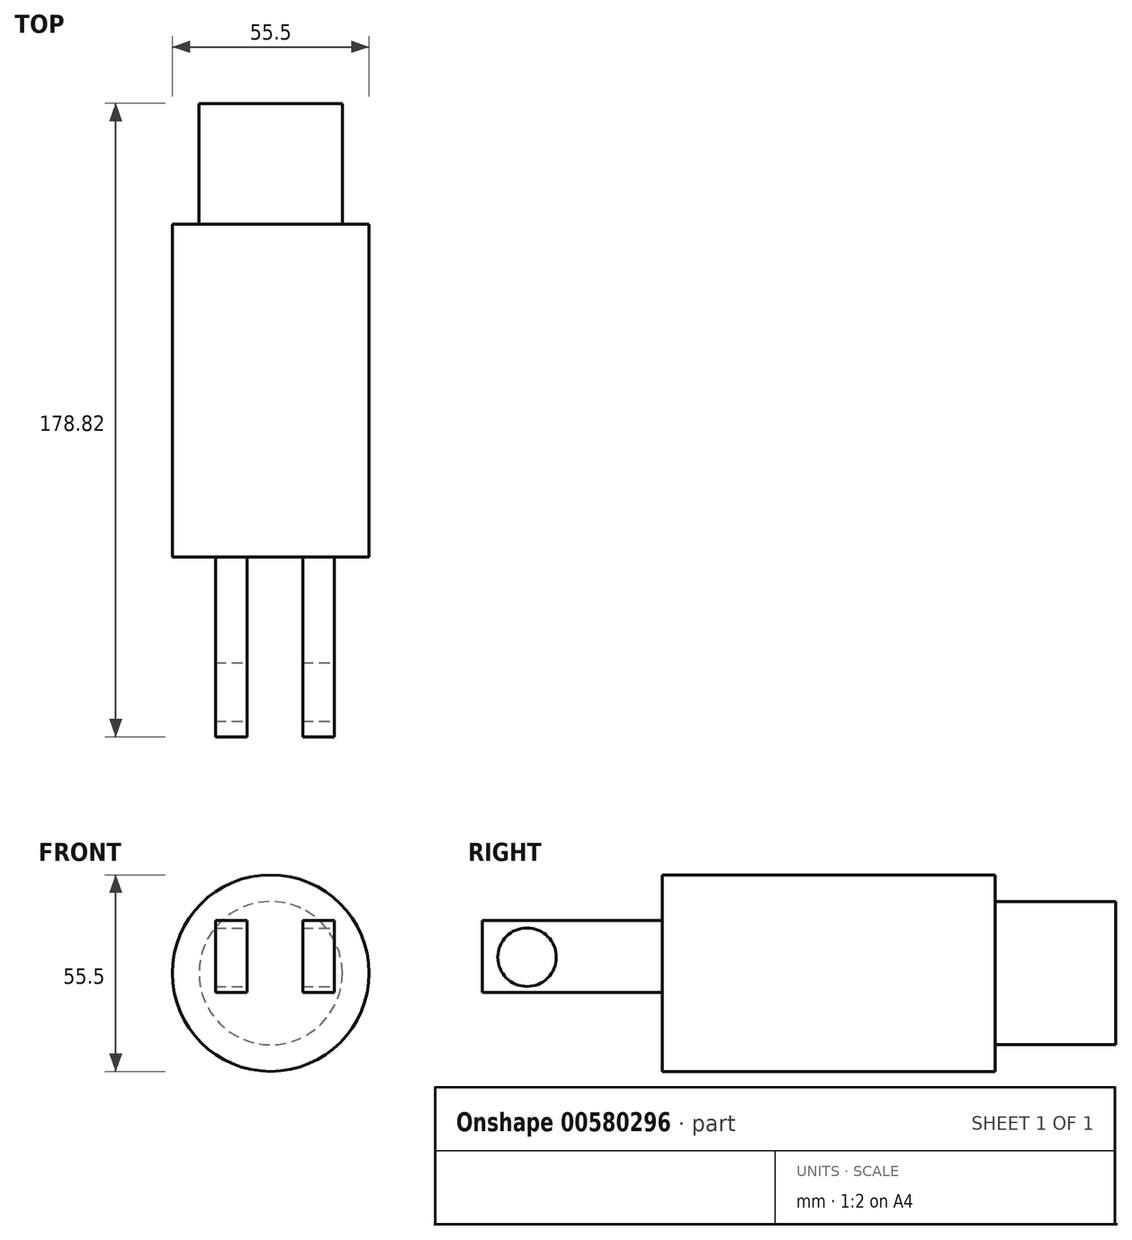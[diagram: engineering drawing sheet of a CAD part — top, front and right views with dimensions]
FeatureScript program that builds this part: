
annotation { "Feature Type Name" : "Feature", "Feature Type Description" : "" }
export const myFeature = defineFeature(function(context is Context, id is Id, definition is map)
    precondition{}
    {
        {
            var Q0;
            Q0=qCreatedBy(makeId("Front.planeOp"),FACE);
            var sketch = newSketch(context, id + "F0", { "sketchPlane" : qUnion([Q0])});
            skCircle(sketch, "E0", {"center": v(0, 0) * mm, "radius": 27.75 * mm});
            skSolve(sketch);
        }
        {
            var Q0;
            Q0 = qSketchRegion(id + "F0", true);
            extrude(context, id + "F1", {"entities" : qUnion([Q0]), "oppositeDirection" : true, "depth" : 93.98 * mm, "offsetDistance" : 25.4 * mm});
        }
        {
            var Q0;
            Q0=makeQuery(id+"F1.opExtrude","CAP_FACE",FACE,{"disambiguationData":[OSD([sQuery(id+"F0.wireOp",EDGE,"E0")])],"isStart":false});
            var sketch = newSketch(context, id + "F2", { "sketchPlane" : qUnion([Q0])});
            skCircle(sketch, "E1", {"center": v(0, 0) * mm, "radius": 20.22 * mm});
            skSolve(sketch);
        }
        {
            var Q0;
            Q0 = qSketchRegion(id + "F2", true);
            extrude(context, id + "F3", {"entities" : qUnion([Q0]), "operationType" : NewBodyOperationType.ADD, "depth" : 34.04 * mm, "offsetDistance" : 25.4 * mm});
        }
        {
            var Q0;
            Q0=qCreatedBy(makeId("Front.planeOp"),FACE);
            var sketch = newSketch(context, id + "F4", { "sketchPlane" : qUnion([Q0])});
            skLineSegment(sketch, "E2", {"start": v(0, 0) * mm, "end": v(-9.1, 0) * mm});
            skLineSegment(sketch, "E3", {"start": v(-9.1, 0) * mm, "end": v(0, 0) * mm});
            skLineSegment(sketch, "E4", {"start": v(0, 0) * mm, "end": v(9.05, 0) * mm});
            skLineSegment(sketch, "E5.bottom", {"start": v(-6.69, -5.45) * mm, "end": v(-15.58, -5.45) * mm});
            skLineSegment(sketch, "E5.top", {"start": v(-6.69, 14.87) * mm, "end": v(-15.58, 14.87) * mm});
            skLineSegment(sketch, "E5.left", {"start": v(-6.69, -5.45) * mm, "end": v(-6.69, 14.87) * mm});
            skLineSegment(sketch, "E5.right", {"start": v(-15.58, -5.45) * mm, "end": v(-15.58, 14.87) * mm});
            skLineSegment(sketch, "E6.bottom", {"start": v(9.05, -5.45) * mm, "end": v(17.94, -5.45) * mm});
            skLineSegment(sketch, "E6.top", {"start": v(9.05, 14.87) * mm, "end": v(17.94, 14.87) * mm});
            skLineSegment(sketch, "E6.left", {"start": v(9.05, -5.45) * mm, "end": v(9.05, 14.87) * mm});
            skLineSegment(sketch, "E6.right", {"start": v(17.94, -5.45) * mm, "end": v(17.94, 14.87) * mm});
            skSolve(sketch);
        }
        {
            var Q0;
            Q0 = qSketchRegion(id + "F4", true);
            extrude(context, id + "F5", {"entities" : qUnion([Q0]), "operationType" : NewBodyOperationType.ADD, "depth" : 50.8 * mm, "offsetDistance" : 25.4 * mm});
        }
        {
            var Q0;
            Q0=qCreatedBy(makeId("Right.planeOp"),FACE);
            var sketch = newSketch(context, id + "F6", { "sketchPlane" : qUnion([Q0])});
            skCircle(sketch, "E7", {"center": v(-38.16, 4.5) * mm, "radius": 8.26 * mm});
            skSolve(sketch);
        }
        {
            var Q0;
            Q0=sQuery(id+"F6.wireOp",EDGE,"E7");
            extrude(context, id + "F7", {"bodyType" : ToolBodyType.SURFACE, "surfaceEntities" : qUnion([Q0]), "depth" : 25.4 * mm, "offsetDistance" : 25.4 * mm, "hasSecondDirection" : true, "secondDirectionOppositeDirection" : true, "secondDirectionDepth" : 25.4 * mm});
        }
        {
            var Q0;
            Q0 = qSketchRegion(id + "F6", true);
            extrude(context, id + "F8", {"entities" : qUnion([Q0]), "operationType" : NewBodyOperationType.REMOVE, "endBound" : BoundingType.SYMMETRIC, "oppositeDirection" : true, "depth" : 76.2 * mm, "offsetDistance" : 25.4 * mm});
        }
    });
